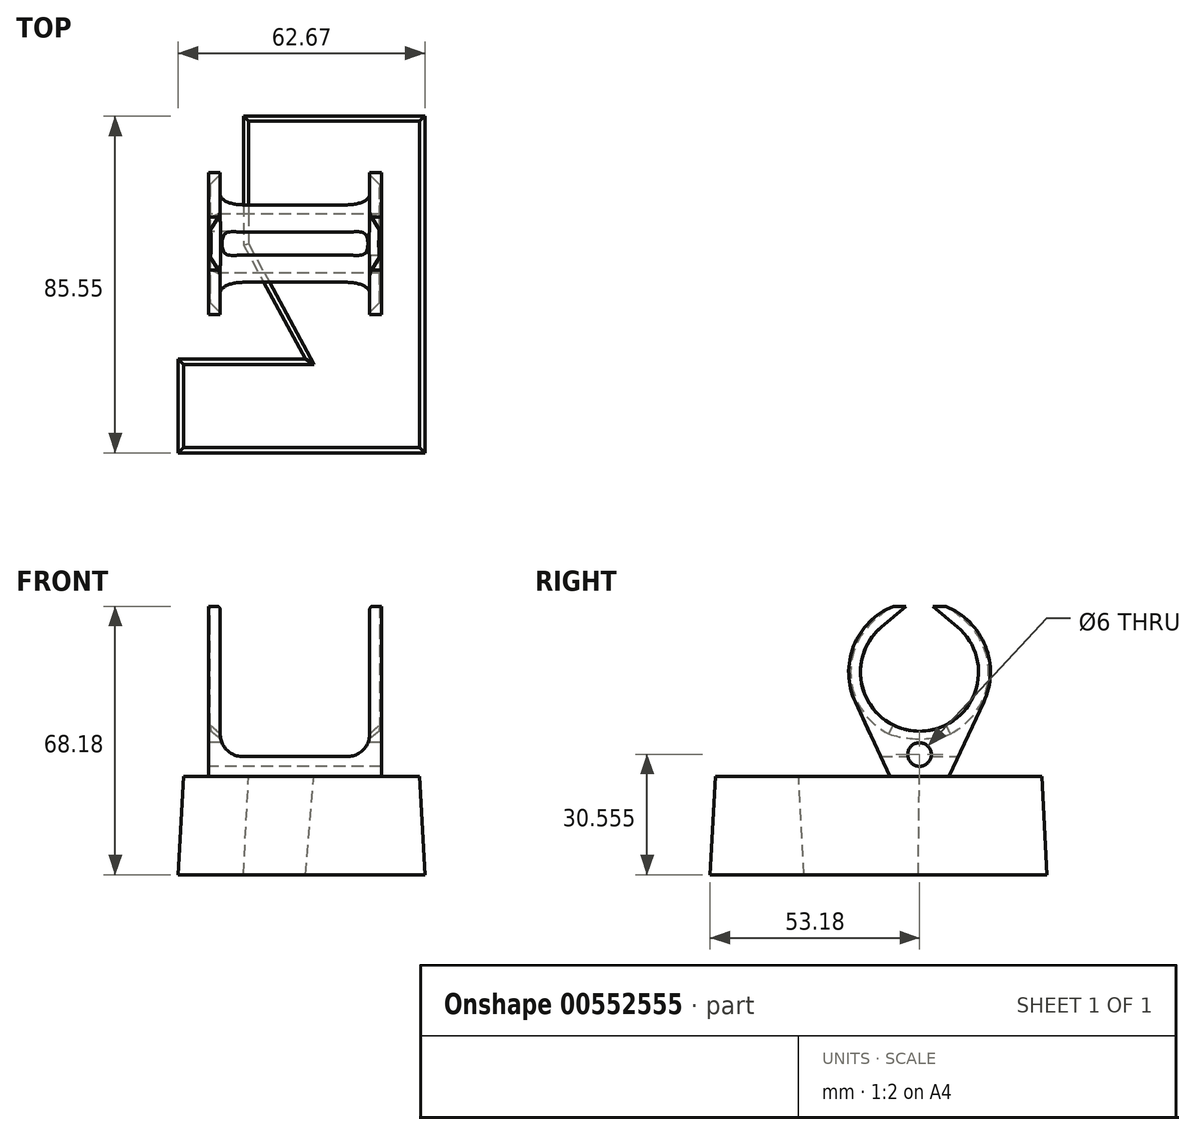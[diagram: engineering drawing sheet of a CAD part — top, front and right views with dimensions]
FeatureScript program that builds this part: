
annotation { "Feature Type Name" : "Feature", "Feature Type Description" : "" }
export const myFeature = defineFeature(function(context is Context, id is Id, definition is map)
    precondition{}
    {
        {
            var Q0;
            Q0=qCreatedBy(makeId("Right.planeOp"),FACE);
            var sketch = newSketch(context, id + "F0", { "sketchPlane" : qUnion([Q0])});
            skArc(sketch, "E0", {"start": v(-9.67, 37.93) * mm, "mid": v(0, 11.46) * mm, "end": v(9.67, 37.93) * mm});
            skArc(sketch, "E1", {"start": v(16.3, 18.84) * mm, "mid": v(16.74, 33.08) * mm, "end": v(6.68, 43.18) * mm});
            skLineSegment(sketch, "E2", {"start": v(-7.5, 0) * mm, "end": v(-16.3, 18.84) * mm});
            skLineSegment(sketch, "E3", {"start": v(7.5, 0) * mm, "end": v(16.3, 18.84) * mm});
            skLineSegment(sketch, "E4", {"start": v(-7.5, 0) * mm, "end": v(7.5, 0) * mm});
            skCircle(sketch, "E5", {"center": v(0, 5.55) * mm, "radius": 3 * mm});
            skLineSegment(sketch, "E6", {"start": v(-3.44, 43.18) * mm, "end": v(-9.67, 37.93) * mm});
            skLineSegment(sketch, "E7", {"start": v(-9.67, 37.93) * mm, "end": v(-3.44, 43.18) * mm});
            skLineSegment(sketch, "E8", {"start": v(9.67, 37.93) * mm, "end": v(3.44, 43.18) * mm});
            skLineSegment(sketch, "E9", {"start": v(-6.68, 43.18) * mm, "end": v(-3.44, 43.18) * mm});
            skLineSegment(sketch, "E10.trimOffspring", {"start": v(3.44, 43.18) * mm, "end": v(6.68, 43.18) * mm});
            skArc(sketch, "E11.trimOffspring", {"start": v(-6.68, 43.18) * mm, "mid": v(-16.74, 33.08) * mm, "end": v(-16.3, 18.84) * mm});
            skPoint(sketch, "E12.orphan", {"position": v(0, 46.08) * mm});
            skSolve(sketch);
        }
        {
            var Q0;
            Q0=makeQuery(id+"F0.imprint","IMPRINT",FACE,{"disambiguationData":[TD([[makeQuery(id+"F0.imprint","IMPRINT",EDGE,{"derivedFrom":sQuery(id+"F0.wireOp",EDGE,"E0")}),-1.0]])]});
            extrude(context, id + "F1", {"entities" : qUnion([Q0]), "depth" : 30 * mm, "offsetDistance" : 25 * mm});
        }
        {
            var Q0;
            Q0 = qSketchRegion(id + "F0", true);
            extrude(context, id + "F2", {"entities" : qUnion([Q0]), "operationType" : NewBodyOperationType.ADD, "oppositeDirection" : true, "depth" : 30 * mm, "offsetDistance" : 25 * mm});
        }
        {
            var Q0;
            Q0=qCreatedBy(makeId("Front.planeOp"),FACE);
            var sketch = newSketch(context, id + "F3", { "sketchPlane" : qUnion([Q0])});
            skLineSegment(sketch, "E13.bottom", {"start": v(-19, 45) * mm, "end": v(19, 45) * mm});
            skLineSegment(sketch, "E13.top", {"start": v(-19, 5) * mm, "end": v(19, 5) * mm});
            skLineSegment(sketch, "E13.left", {"start": v(-22, 45) * mm, "end": v(-22, 5) * mm});
            skLineSegment(sketch, "E13.right", {"start": v(22, 45) * mm, "end": v(22, 5) * mm});
            skLineSegment(sketch, "E14.left", {"start": v(-19, 45) * mm, "end": v(-19, 5) * mm});
            skLineSegment(sketch, "E14.right", {"start": v(19, 45) * mm, "end": v(19, 5) * mm});
            skLineSegment(sketch, "E15", {"start": v(-22, 45) * mm, "end": v(-36.05, 50.2) * mm});
            skLineSegment(sketch, "E16", {"start": v(-36.05, 50.2) * mm, "end": v(-36.05, -3.86) * mm});
            skLineSegment(sketch, "E17", {"start": v(-36.05, -3.86) * mm, "end": v(-22, -5.02) * mm});
            skLineSegment(sketch, "E18", {"start": v(-22, -5.02) * mm, "end": v(-22, 5) * mm});
            skLineSegment(sketch, "E19", {"start": v(22, 5) * mm, "end": v(22, -7.34) * mm});
            skLineSegment(sketch, "E20", {"start": v(22, -7.34) * mm, "end": v(40.2, -3.73) * mm});
            skLineSegment(sketch, "E21", {"start": v(40.2, -3.73) * mm, "end": v(40.2, 48.53) * mm});
            skLineSegment(sketch, "E22", {"start": v(40.2, 48.53) * mm, "end": v(22, 45) * mm});
            skSolve(sketch);
        }
        {
            var Q0;
            Q0 = qSketchRegion(id + "F3", true);
            extrude(context, id + "F4", {"entities" : qUnion([Q0]), "operationType" : NewBodyOperationType.REMOVE, "endBound" : BoundingType.SYMMETRIC, "depth" : 36.6 * mm, "offsetDistance" : 25 * mm});
        }
        {
            var Q0;
            {var subQ1=sQuery(id+"F0.wireOp",EDGE,"E2");var subQ2=sQuery(id+"F3.wireOp",EDGE,"E14.left");var subQ3=sQuery(id+"F3.wireOp",EDGE,"E13.top");Q0=makeQuery(id+"F4.boolean.opBoolean","COPY",EDGE,{"disambiguationData":[TD([makeQuery(id+"F1.opExtrude","SWEPT_FACE",FACE,{"disambiguationData":[OSD([subQ1])]})])],"derivedFrom":makeQuery(id+"F4.opExtrude","SWEPT_EDGE",EDGE,{"disambiguationData":[OSD([subQ3,subQ2])]})});}
            var Q1;
            {var subQ1=sQuery(id+"F0.wireOp",EDGE,"E2");var subQ2=sQuery(id+"F3.wireOp",EDGE,"E13.top");var subQ3=sQuery(id+"F3.wireOp",EDGE,"E14.right");Q1=makeQuery(id+"F4.boolean.opBoolean","COPY",EDGE,{"disambiguationData":[TD([makeQuery(id+"F1.opExtrude","SWEPT_FACE",FACE,{"disambiguationData":[OSD([subQ1])]})])],"derivedFrom":makeQuery(id+"F4.opExtrude","SWEPT_EDGE",EDGE,{"disambiguationData":[OSD([subQ2,subQ3])]})});}
            fillet(context, id + "F5", {"entities" : qUnion([Q0, Q1]), "radius" : 5.8 * mm, "tangentPropagation" : true, "allowEdgeOverflow" : false});
        }
        {
            var Q0;
            {var subQ0=sQuery(id+"F0.wireOp",EDGE,"E0");Q0=makeQuery(id+"F4.boolean.opBoolean","INTERSECT",EDGE,{"derivedFrom":[makeQuery(id+"F2.boolean.opBoolean","MERGE",FACE,{"derivedFrom":[makeQuery(id+"F1.opExtrude","SWEPT_FACE",FACE,{"disambiguationData":[OSD([subQ0])]}),makeQuery(id+"F2.opExtrude","SWEPT_FACE",FACE,{"disambiguationData":[OSD([subQ0])]})]}),makeQuery(id+"F4.opExtrude","SWEPT_FACE",FACE,{"disambiguationData":[OSD([sQuery(id+"F3.wireOp",EDGE,"E14.right")])]})]});}
            var Q1;
            {var subQ0=sQuery(id+"F0.wireOp",EDGE,"E0");Q1=makeQuery(id+"F4.boolean.opBoolean","INTERSECT",EDGE,{"derivedFrom":[makeQuery(id+"F2.boolean.opBoolean","MERGE",FACE,{"derivedFrom":[makeQuery(id+"F1.opExtrude","SWEPT_FACE",FACE,{"disambiguationData":[OSD([subQ0])]}),makeQuery(id+"F2.opExtrude","SWEPT_FACE",FACE,{"disambiguationData":[OSD([subQ0])]})]}),makeQuery(id+"F4.opExtrude","SWEPT_FACE",FACE,{"disambiguationData":[OSD([sQuery(id+"F3.wireOp",EDGE,"E14.left")])]})]});}
            chamfer(context, id + "F6", {"entities" : qUnion([Q0, Q1]), "width" : 2.5 * mm, "tangentPropagation" : true});
        }
        {
            var Q0;
            {var subQ0=sQuery(id+"F0.wireOp",EDGE,"E4");Q0=makeQuery(id+"F2.boolean.opBoolean","MERGE",FACE,{"derivedFrom":[makeQuery(id+"F1.opExtrude","SWEPT_FACE",FACE,{"disambiguationData":[OSD([subQ0])]}),makeQuery(id+"F2.opExtrude","SWEPT_FACE",FACE,{"disambiguationData":[OSD([subQ0])]})]});}
            var sketch = newSketch(context, id + "F7", { "sketchPlane" : qUnion([Q0])});
            skLineSegment(sketch, "E23.bottom", {"start": v(-11.78, 0) * mm, "end": v(31.7, 0) * mm});
            skLineSegment(sketch, "E23.top", {"start": v(-11.78, -31.06) * mm, "end": v(31.7, -31.06) * mm});
            skLineSegment(sketch, "E23.left", {"start": v(-11.78, 0) * mm, "end": v(-11.78, -31.06) * mm});
            skLineSegment(sketch, "E23.right", {"start": v(31.7, 0) * mm, "end": v(31.7, -31.06) * mm});
            skLineSegment(sketch, "E24", {"start": v(31.7, 0) * mm, "end": v(31.7, 51.87) * mm});
            skLineSegment(sketch, "E25", {"start": v(31.7, 51.87) * mm, "end": v(-28.34, 51.87) * mm});
            skLineSegment(sketch, "E26", {"start": v(-28.34, 51.87) * mm, "end": v(-28.34, 30.67) * mm});
            skLineSegment(sketch, "E27", {"start": v(-28.34, 30.67) * mm, "end": v(4.84, 30.67) * mm});
            skLineSegment(sketch, "E28", {"start": v(4.84, 30.67) * mm, "end": v(-11.78, 0) * mm});
            skSolve(sketch);
        }
        {
            var Q0;
            Q0 = qSketchRegion(id + "F7", true);
            extrude(context, id + "F8", {"entities" : qUnion([Q0]), "operationType" : NewBodyOperationType.ADD, "depth" : 25 * mm, "offsetDistance" : 25 * mm, "hasDraft" : true, "draftAngle" : 3 * degree});
        }
    });
